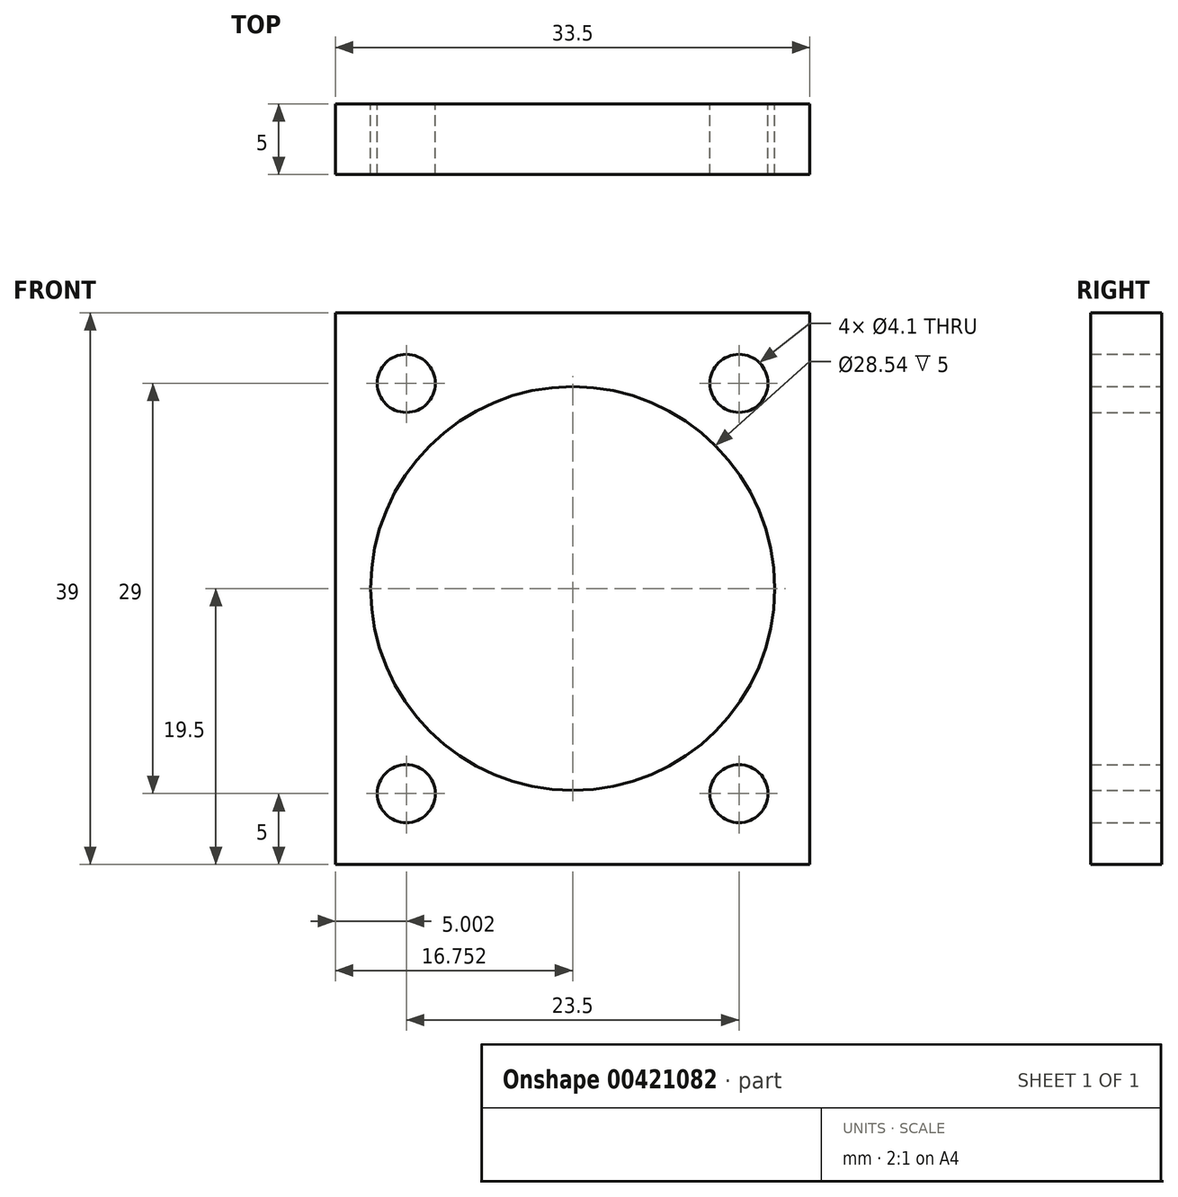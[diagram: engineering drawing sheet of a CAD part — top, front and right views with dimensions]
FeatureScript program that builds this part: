
annotation { "Feature Type Name" : "Feature", "Feature Type Description" : "" }
export const myFeature = defineFeature(function(context is Context, id is Id, definition is map)
    precondition{}
    {
        {
            var Q0;
            Q0=qCreatedBy(makeId("Front.planeOp"),FACE);
            var sketch = newSketch(context, id + "F0", { "sketchPlane" : qUnion([Q0])});
            skLineSegment(sketch, "E0.bottom", {"start": v(-48.78, 5) * mm, "end": v(-15.28, 5) * mm});
            skLineSegment(sketch, "E0.top", {"start": v(-48.78, -34) * mm, "end": v(-15.28, -34) * mm});
            skLineSegment(sketch, "E0.left", {"start": v(-48.78, 5) * mm, "end": v(-48.78, -34) * mm});
            skLineSegment(sketch, "E0.right", {"start": v(-15.28, 5) * mm, "end": v(-15.28, -34) * mm});
            skCircle(sketch, "E1", {"center": v(-32.03, -14.5) * mm, "radius": 14.27 * mm});
            skCircle(sketch, "E2", {"center": v(-43.78, 0) * mm, "radius": 2.05 * mm});
            skCircle(sketch, "E3", {"center": v(-20.28, 0) * mm, "radius": 2.05 * mm});
            skCircle(sketch, "E4", {"center": v(-20.28, -29) * mm, "radius": 2.05 * mm});
            skCircle(sketch, "E5", {"center": v(-43.78, -29) * mm, "radius": 2.05 * mm});
            skSolve(sketch);
        }
        {
            var Q0;
            Q0=makeQuery(id+"F0.imprint","IMPRINT",FACE,{"disambiguationData":[TD([[makeQuery(id+"F0.imprint","IMPRINT",EDGE,{"derivedFrom":sQuery(id+"F0.wireOp",EDGE,"E0.bottom")}),-1.0]])]});
            extrude(context, id + "F1", {"entities" : qUnion([Q0]), "depth" : 5 * mm});
        }
    });
